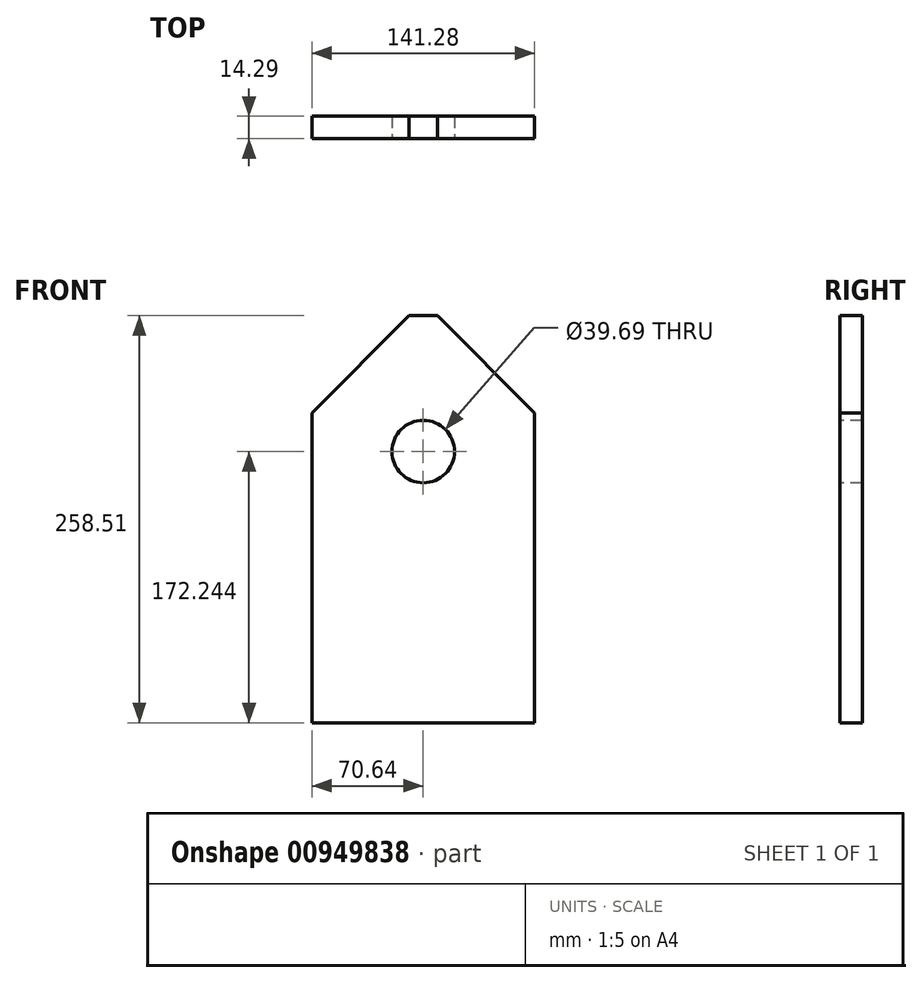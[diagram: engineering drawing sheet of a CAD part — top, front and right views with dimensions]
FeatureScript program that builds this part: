
annotation { "Feature Type Name" : "Feature", "Feature Type Description" : "" }
export const myFeature = defineFeature(function(context is Context, id is Id, definition is map)
    precondition{}
    {
        {
            var Q0;
            Q0=qCreatedBy(makeId("Front.planeOp"),FACE);
            var sketch = newSketch(context, id + "F0", { "sketchPlane" : qUnion([Q0])});
            skLineSegment(sketch, "E0", {"start": v(-70.64, 0) * mm, "end": v(-70.64, 196.85) * mm});
            skLineSegment(sketch, "E1", {"start": v(-70.64, 196.85) * mm, "end": v(0, 267.5) * mm});
            skLineSegment(sketch, "E2", {"start": v(0, 267.5) * mm, "end": v(70.64, 196.85) * mm});
            skLineSegment(sketch, "E3", {"start": v(70.64, 196.85) * mm, "end": v(70.64, 0) * mm});
            skLineSegment(sketch, "E4", {"start": v(70.64, 0) * mm, "end": v(-70.64, 0) * mm});
            skSolve(sketch);
        }
        {
            var Q0;
            Q0=makeQuery(id+"F0.imprint","IMPRINT",FACE,{"disambiguationData":[TD([[makeQuery(id+"F0.imprint","IMPRINT",EDGE,{"derivedFrom":sQuery(id+"F0.wireOp",EDGE,"E0")}),-1.0]])]});
            extrude(context, id + "F1", {"entities" : qUnion([Q0]), "depth" : 14.29 * mm, "offsetDistance" : 25.4 * mm});
        }
        {
            var Q0;
            Q0=makeQuery(id+"F1.opExtrude","CAP_FACE",FACE,{"disambiguationData":[OSD([sQuery(id+"F0.wireOp",EDGE,"E0"),sQuery(id+"F0.wireOp",EDGE,"E1"),sQuery(id+"F0.wireOp",EDGE,"E2"),sQuery(id+"F0.wireOp",EDGE,"E3"),sQuery(id+"F0.wireOp",EDGE,"E4")])],"isStart":false});
            var sketch = newSketch(context, id + "F2", { "sketchPlane" : qUnion([Q0])});
            skCircle(sketch, "E5", {"center": v(0, 172.24) * mm, "radius": 19.84 * mm});
            skSolve(sketch);
        }
        {
            var Q0;
            Q0=qSketchRegion(id+"F0",true);
            var Q1;
            Q1=qSketchRegion(id+"F2",true);
            extrude(context, id + "F3", {"entities" : qUnion([Q0, Q1]), "operationType" : NewBodyOperationType.REMOVE, "endBound" : BoundingType.THROUGH_ALL, "oppositeDirection" : true, "depth" : 25.4 * mm, "offsetDistance" : 25.4 * mm});
        }
        {
            var Q0;
            Q0=makeQuery(id+"F1.opExtrude","SWEPT_EDGE",EDGE,{"disambiguationData":[OSD([sQuery(id+"F0.wireOp",EDGE,"E1"),sQuery(id+"F0.wireOp",EDGE,"E2")])]});
            chamfer(context, id + "F4", {"entities" : qUnion([Q0]), "width" : 12.7 * mm, "tangentPropagation" : true});
        }
        {
            var Q0;
            Q0=qSketchRegion(id+"F2",true);
            extrude(context, id + "F5", {"entities" : qUnion([Q0]), "operationType" : NewBodyOperationType.REMOVE, "endBound" : BoundingType.THROUGH_ALL, "oppositeDirection" : true, "depth" : 25.4 * mm, "offsetDistance" : 25.4 * mm});
        }
    });
